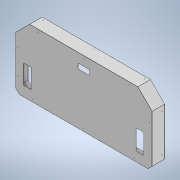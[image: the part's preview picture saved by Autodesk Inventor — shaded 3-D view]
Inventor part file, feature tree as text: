
AUTODESK INVENTOR PART (.ipt)
format: ipt  version: 2022.1 (Build 261234000, 234)  size: 632,832 bytes
history: native  units: mm
features: reference x23, other x16, sketch x10, hole x5, projected_geometry x5, sheet_metal_op x4, chamfer x3
ambient origin geometry x8: Origin, YZ Plane, XZ Plane, XY Plane, X Axis, Y Axis, Z Axis, Center Point
bodies: Solid1 (feature_tree)
feature tree (66):
  sheet_metal_op  "Face1"
  chamfer  "Corner Round1"
  sheet_metal_op  "Flange1"
  chamfer  "Corner Round2"
  chamfer  "Corner Round3"
  hole  "Hole1"  [1 undecoded]
  sketch  "Sketch8"  dims[d17=0.25mm]
  hole  "Hole2"  [1 undecoded]
  hole  "Hole3"  [1 undecoded]
  hole  "Hole4"  [1 undecoded]
  hole  "Hole5"  [1 undecoded]
  sketch  "Sketch1"  dims[d0=0.5mm d1=5.0mm]
  reference  "Reference1"
  reference  "Reference2"
  reference  "Reference3"
  reference  "Reference4"
  reference  "Reference5"
  reference  "Reference6"
  reference  "Reference7"
  reference  "Reference8"
  reference  "Reference9"
  other  "Plate1"
  sketch  "Sketch2"  dims[d2=5.0mm d3=0.5mm]
  reference  "Reference10"
  reference  "Reference11"
  reference  "Reference12"
  reference  "Reference13"
  sketch  "Sketch3"  dims[d4=0.0mm d5=5.0mm]
  other  "Plate2"
  sheet_metal_op  "Bend1"
  sheet_metal_op  "Corner1"
  sketch  "Sketch5"  dims[d11=35.0mm d13=35.0mm]
  reference  "Reference18"
  reference  "Reference19"
  reference  "Reference20"
  reference  "Reference21"
  reference  "Reference22"
  reference  "Reference23"
  reference  "Reference24"
  reference  "Reference25"
  sketch  "Sketch6"  dims[d14=35.0mm d15=35.0mm]
  sketch  "Sketch7"  dims[d16=0.5mm]
  reference  "Reference26"
  reference  "Reference27"
  sketch  "Sketch9"  dims[d18=1.0mm]
  sketch  "Sketch10"  dims[d19=0.5mm]
  sketch  "Sketch11"  dims[d20=100.0mm d21=90.0deg d22=0.5mm d23=2.0mm d24=0.5mm d25=0.5mm d30=90.0mm d31=40.0mm d32=0.5mm d33=0.0mm d34=3.0mm d35=0.5mm d36=0.0mm d37=6.0mm d38=200.0mm d39=3.4mm d40=6.0mm d41=6.3mm d42=2.0mm d43=90.0deg d44=0.5mm d45=20.594885mm d46=800.0mm d47=20.0mm d48=20.0mm d49=300.0mm d50=3.4mm d51=8.0mm d52=6.3mm d53=4.775mm d54=90.0deg d55=0.5mm d56=20.594885mm d57=3.4mm d58=6.0mm d59=6.3mm d60=2.0mm d61=90.0deg d62=8.0mm d63=20.594885mm d64=3.4mm d65=6.0mm d66=6.3mm d67=2.0mm d68=90.0deg d69=8.0mm d70=20.594885mm d71=20.0mm d72=3.4mm d73=6.0mm d74=6.3mm d75=2.0mm d76=90.0deg d77=8.0mm d78=20.594885mm]
  projected_geometry  "Projected Loop1"
  projected_geometry  "Projected Loop2"
  projected_geometry  "Projected Loop3"
  projected_geometry  "Projected Loop4"
  projected_geometry  "Projected Loop5"
  other  "Cut1"
  other  "Cut2"
  other  "Cut3"
  other  "<userpath>\Desktop\PDM\ProyectoRobotPallet\RobotPallet.iam"
  other  "RobotPallet.iam"
  other  "EstructuraInferior - Soldadura:1"
  other  "Frame_Base:1"
  other  "ISO 12633-2 40x40x5 - 2899.41:1"
  other  "BL Motor + Encoder + Gearbox + Rueda:2"
  other  "Rueda:1"
  other  "Exterior_Rueda:1"
  other  "BL Motor + Encoder + Gearbox + Rueda:1"
  other  "PlanchaBaseInferior:1"
  other  "Definición1"
note: 5 required parameter values undecoded (feature->parameter linkage not recoverable at this tier; creation-order binding heuristic only, values carry confidence <= 0.55)
